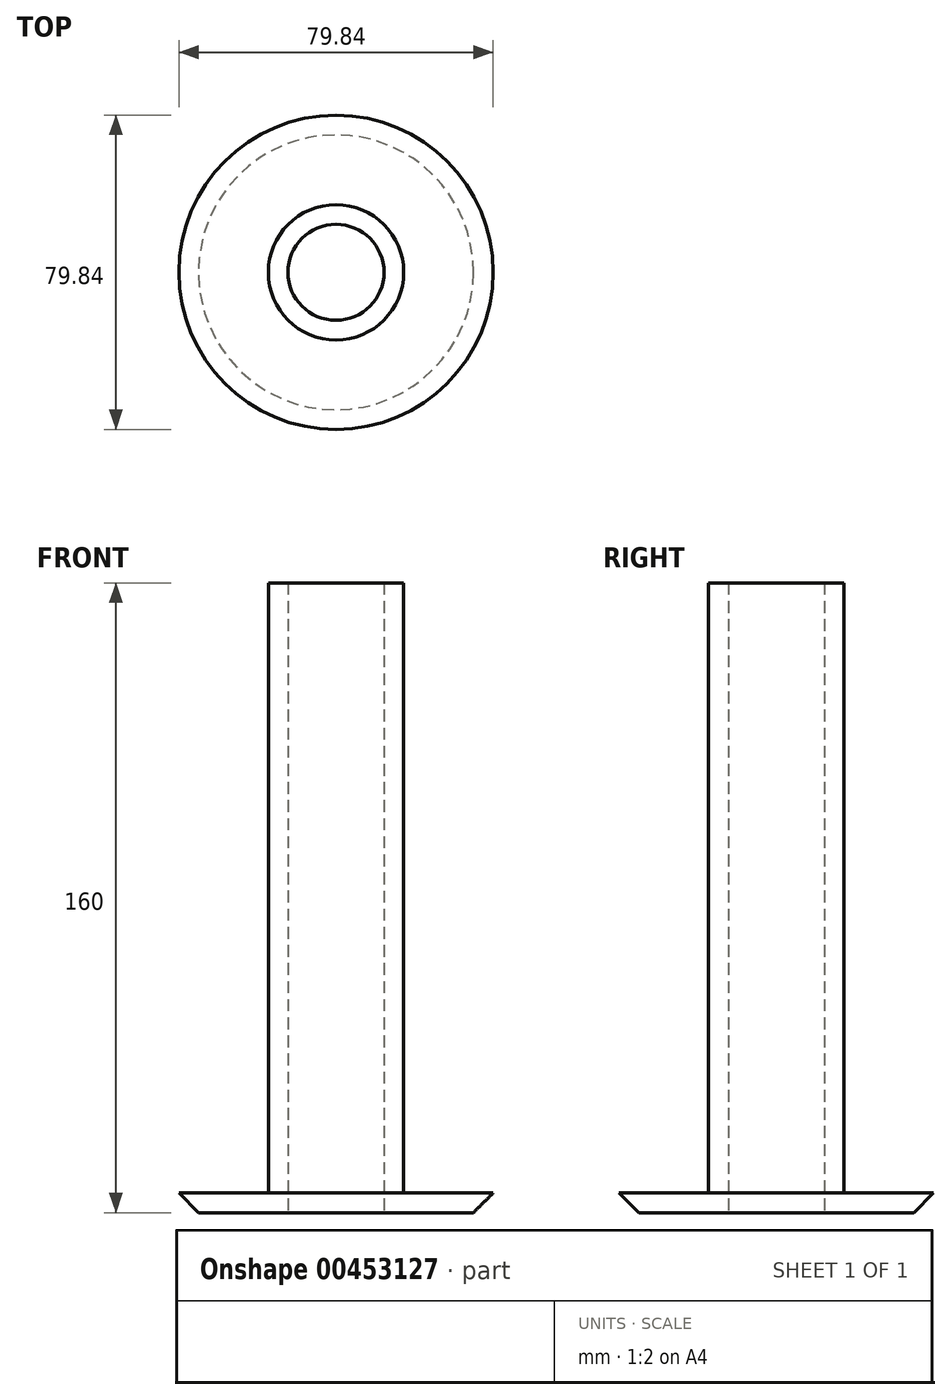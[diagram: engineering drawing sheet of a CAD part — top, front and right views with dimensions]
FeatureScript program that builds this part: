
annotation { "Feature Type Name" : "Feature", "Feature Type Description" : "" }
export const myFeature = defineFeature(function(context is Context, id is Id, definition is map)
    precondition{}
    {
        {
            var Q0;
            Q0=qCreatedBy(makeId("Top.planeOp"),FACE);
            var sketch = newSketch(context, id + "F0", { "sketchPlane" : qUnion([Q0])});
            skCircle(sketch, "E0", {"center": v(0, 0) * mm, "radius": 12.2 * mm});
            skSolve(sketch);
        }
        {
            var Q0;
            Q0=qCreatedBy(makeId("Top.planeOp"),FACE);
            var sketch = newSketch(context, id + "F1", { "sketchPlane" : qUnion([Q0])});
            skCircle(sketch, "E1", {"center": v(0, 0) * mm, "radius": 17.2 * mm});
            skSolve(sketch);
        }
        {
            var Q0;
            Q0=qCreatedBy(makeId("Top.planeOp"),FACE);
            var sketch = newSketch(context, id + "F2", { "sketchPlane" : qUnion([Q0])});
            skLineSegment(sketch, "E2.bottom", {"start": v(0, 40) * mm, "end": v(0, 40) * mm});
            skLineSegment(sketch, "E2.top", {"start": v(0, -40) * mm, "end": v(0, -40) * mm});
            skLineSegment(sketch, "E2.left", {"start": v(40, 0) * mm, "end": v(40, 0) * mm});
            skLineSegment(sketch, "E2.right", {"start": v(-40, 0) * mm, "end": v(-40, 0) * mm});
            skPoint(sketch, "E2.middle", {"position": v(0, 0) * mm});
            skPoint(sketch, "E3.visualSharp", {"position": v(-40, 40) * mm});
            skArc(sketch, "E3.filletArc", {"start": v(0, 40) * mm, "mid": v(-28.28, 28.28) * mm, "end": v(-40, 0) * mm});
            skPoint(sketch, "E4.visualSharp", {"position": v(-40, -40) * mm});
            skArc(sketch, "E4.filletArc", {"start": v(-40, 0) * mm, "mid": v(-28.28, -28.28) * mm, "end": v(0, -40) * mm});
            skPoint(sketch, "E5.visualSharp", {"position": v(40, -40) * mm});
            skArc(sketch, "E5.filletArc", {"start": v(0, -40) * mm, "mid": v(28.28, -28.28) * mm, "end": v(40, 0) * mm});
            skPoint(sketch, "E6.visualSharp", {"position": v(40, 40) * mm});
            skArc(sketch, "E6.filletArc", {"start": v(40, 0) * mm, "mid": v(28.28, 28.28) * mm, "end": v(0, 40) * mm});
            skSolve(sketch);
        }
        {
            var Q0;
            Q0 = qSketchRegion(id + "F2", true);
            extrude(context, id + "F3", {"entities" : qUnion([Q0]), "depth" : 5 * mm});
        }
        {
            var Q0;
            Q0 = qSketchRegion(id + "F1", true);
            extrude(context, id + "F4", {"entities" : qUnion([Q0]), "operationType" : NewBodyOperationType.ADD, "depth" : 160 * mm});
        }
        {
            var Q0;
            Q0 = qSketchRegion(id + "F0", true);
            extrude(context, id + "F5", {"entities" : qUnion([Q0]), "operationType" : NewBodyOperationType.REMOVE, "depth" : 160 * mm});
        }
        {
            var Q0;
            Q0=makeQuery(id+"F3.opExtrude","CAP_EDGE",EDGE,{"disambiguationData":[OSD([sQuery(id+"F2.wireOp",EDGE,"E3.filletArc"),sQuery(id+"F2.wireOp",EDGE,"E4.filletArc"),sQuery(id+"F2.wireOp",EDGE,"E5.filletArc"),sQuery(id+"F2.wireOp",EDGE,"E6.filletArc")])],"isStart":true});
            chamfer(context, id + "F6", {"entities" : qUnion([Q0]), "width" : 5.08 * mm, "tangentPropagation" : true});
        }
    });
